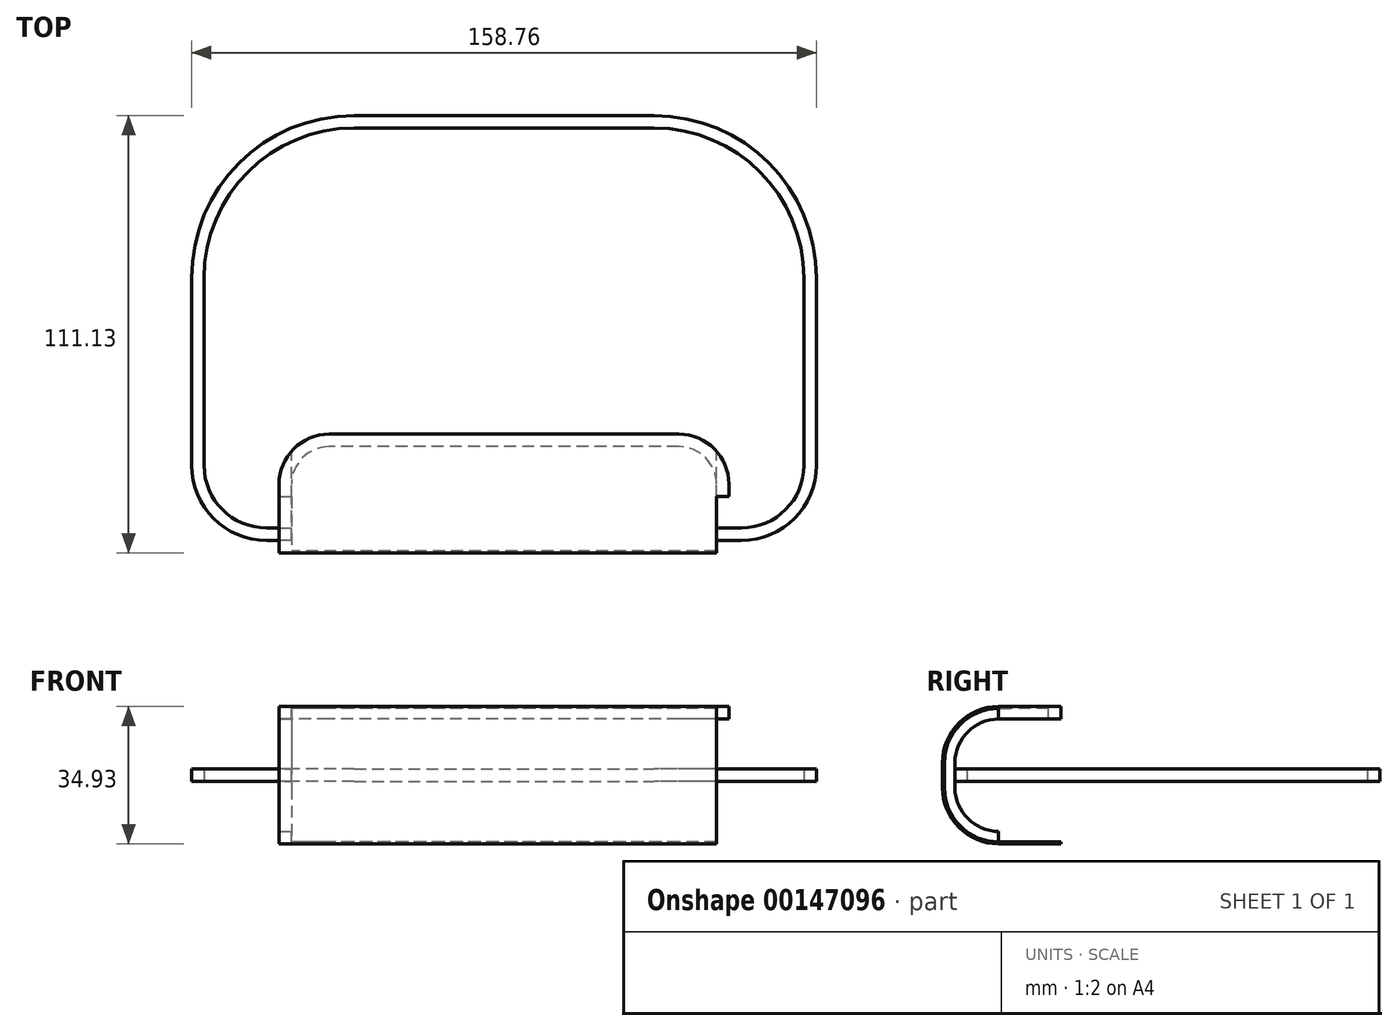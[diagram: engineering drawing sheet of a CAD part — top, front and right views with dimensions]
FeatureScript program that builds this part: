
annotation { "Feature Type Name" : "Feature", "Feature Type Description" : "" }
export const myFeature = defineFeature(function(context is Context, id is Id, definition is map)
    precondition{}
    {
        {
            var Q0;
            Q0=qCreatedBy(makeId("Top.planeOp"),FACE);
            var sketch = newSketch(context, id + "F0", { "sketchPlane" : qUnion([Q0])});
            skLineSegment(sketch, "E0.bottom", {"start": v(15.88, 0) * mm, "end": v(136.53, 0) * mm});
            skLineSegment(sketch, "E0.top", {"start": v(38.1, 101.6) * mm, "end": v(114.3, 101.6) * mm});
            skLineSegment(sketch, "E0.left", {"start": v(0, 15.87) * mm, "end": v(0, 63.5) * mm});
            skLineSegment(sketch, "E0.right", {"start": v(152.4, 15.88) * mm, "end": v(152.4, 63.5) * mm});
            skPoint(sketch, "E1.visualSharp", {"position": v(0, 101.6) * mm});
            skArc(sketch, "E1.filletArc", {"start": v(38.1, 101.6) * mm, "mid": v(11.16, 90.44) * mm, "end": v(0, 63.5) * mm});
            skPoint(sketch, "E2.visualSharp", {"position": v(152.4, 101.6) * mm});
            skArc(sketch, "E2.filletArc", {"start": v(152.4, 63.5) * mm, "mid": v(141.24, 90.44) * mm, "end": v(114.3, 101.6) * mm});
            skPoint(sketch, "E3.visualSharp", {"position": v(0, 0) * mm});
            skArc(sketch, "E3.filletArc", {"start": v(0, 15.87) * mm, "mid": v(4.65, 4.65) * mm, "end": v(15.87, 0) * mm});
            skPoint(sketch, "E4.visualSharp", {"position": v(152.4, 0) * mm});
            skArc(sketch, "E4.filletArc", {"start": v(136.53, 0) * mm, "mid": v(147.75, 4.65) * mm, "end": v(152.4, 15.88) * mm});
            skArc(sketch, "E5.0", {"start": v(38.1, 104.78) * mm, "mid": v(8.91, 92.69) * mm, "end": v(-3.18, 63.5) * mm});
            skArc(sketch, "E6.0", {"start": v(155.58, 63.5) * mm, "mid": v(143.49, 92.69) * mm, "end": v(114.3, 104.78) * mm});
            skArc(sketch, "E7.0", {"start": v(136.53, -3.18) * mm, "mid": v(150, 2.4) * mm, "end": v(155.58, 15.87) * mm});
            skArc(sketch, "E8.0", {"start": v(-3.18, 15.88) * mm, "mid": v(2.4, 2.4) * mm, "end": v(15.87, -3.18) * mm});
            skLineSegment(sketch, "E9", {"start": v(38.1, 104.78) * mm, "end": v(114.3, 104.78) * mm});
            skLineSegment(sketch, "E10", {"start": v(155.58, 63.5) * mm, "end": v(155.58, 15.87) * mm});
            skLineSegment(sketch, "E11", {"start": v(136.53, -3.18) * mm, "end": v(15.88, -3.18) * mm});
            skLineSegment(sketch, "E12", {"start": v(-3.18, 15.88) * mm, "end": v(-3.18, 63.5) * mm});
            skSolve(sketch);
        }
        {
            var Q0;
            Q0 = qSketchRegion(id + "F0", true);
            extrude(context, id + "F1", {"entities" : qUnion([Q0]), "depth" : 3.17 * mm});
        }
        {
            var Q0;
            Q0=makeQuery(id+"F1.opExtrude","CAP_FACE",FACE,{"disambiguationData":[OSD([sQuery(id+"F0.wireOp",EDGE,"E0.bottom"),sQuery(id+"F0.wireOp",EDGE,"E0.top"),sQuery(id+"F0.wireOp",EDGE,"E0.left"),sQuery(id+"F0.wireOp",EDGE,"E0.right"),sQuery(id+"F0.wireOp",EDGE,"E1.filletArc"),sQuery(id+"F0.wireOp",EDGE,"E2.filletArc"),sQuery(id+"F0.wireOp",EDGE,"E3.filletArc"),sQuery(id+"F0.wireOp",EDGE,"E4.filletArc"),sQuery(id+"F0.wireOp",EDGE,"E5.0"),sQuery(id+"F0.wireOp",EDGE,"E6.0"),sQuery(id+"F0.wireOp",EDGE,"E7.0"),sQuery(id+"F0.wireOp",EDGE,"E8.0"),sQuery(id+"F0.wireOp",EDGE,"E9"),sQuery(id+"F0.wireOp",EDGE,"E10"),sQuery(id+"F0.wireOp",EDGE,"E11"),sQuery(id+"F0.wireOp",EDGE,"E12")])],"isStart":false});
            var sketch = newSketch(context, id + "F2", { "sketchPlane" : qUnion([Q0])});
            skLineSegment(sketch, "E13.bottom", {"start": v(22.23, -3.18) * mm, "end": v(130.18, -3.18) * mm});
            skLineSegment(sketch, "E13.top", {"start": v(22.23, 0) * mm, "end": v(130.18, 0) * mm});
            skLineSegment(sketch, "E13.left", {"start": v(22.23, -3.18) * mm, "end": v(22.23, 0) * mm});
            skLineSegment(sketch, "E13.right", {"start": v(130.18, -3.18) * mm, "end": v(130.18, 0) * mm});
            skLineSegment(sketch, "E14", {"start": v(76.2, 101.6) * mm, "end": v(76.2, 0) * mm, "construction": true});
            skSolve(sketch);
        }
        {
            var Q0;
            Q0=makeQuery(id+"F2.imprint","IMPRINT",FACE,{"disambiguationData":[TD([[makeQuery(id+"F2.imprint","IMPRINT",EDGE,{"derivedFrom":sQuery(id+"F2.wireOp",EDGE,"E13.bottom")}),-1.0]])]});
            extrude(context, id + "F3", {"entities" : qUnion([Q0]), "operationType" : NewBodyOperationType.REMOVE, "endBound" : BoundingType.THROUGH_ALL, "oppositeDirection" : true, "depth" : 25.4 * mm});
        }
        {
            var Q0;
            Q0=makeQuery(id+"F3.boolean.opBoolean","COPY",FACE,{"derivedFrom":makeQuery(id+"F3.opExtrude","SWEPT_FACE",FACE,{"disambiguationData":[OSD([sQuery(id+"F2.wireOp",EDGE,"E13.left")])]})});
            var sketch = newSketch(context, id + "F4", { "sketchPlane" : qUnion([Q0])});
            skLineSegment(sketch, "E15", {"start": v(-3.18, 4.76) * mm, "end": v(-3.18, -1.59) * mm});
            skLineSegment(sketch, "E16", {"start": v(7.94, -12.7) * mm, "end": v(7.94, -12.7) * mm});
            skLineSegment(sketch, "E17", {"start": v(7.94, 15.88) * mm, "end": v(7.94, 15.88) * mm});
            skLineSegment(sketch, "E18", {"start": v(7.94, 15.88) * mm, "end": v(7.94, -12.7) * mm, "construction": true});
            skLineSegment(sketch, "E19", {"start": v(7.94, 15.88) * mm, "end": v(7.94, 19.05) * mm});
            skLineSegment(sketch, "E20", {"start": v(7.94, 19.05) * mm, "end": v(7.94, 19.05) * mm});
            skLineSegment(sketch, "E21", {"start": v(-6.35, 4.76) * mm, "end": v(-6.35, -1.59) * mm});
            skLineSegment(sketch, "E22", {"start": v(7.94, -15.88) * mm, "end": v(7.94, -15.88) * mm});
            skLineSegment(sketch, "E23", {"start": v(7.94, -15.88) * mm, "end": v(7.94, -12.7) * mm});
            skPoint(sketch, "E24.visualSharp", {"position": v(-3.18, 15.87) * mm});
            skArc(sketch, "E24.filletArc", {"start": v(7.94, 15.88) * mm, "mid": v(0.08, 12.62) * mm, "end": v(-3.18, 4.76) * mm});
            skPoint(sketch, "E25.visualSharp", {"position": v(-3.18, -12.7) * mm});
            skArc(sketch, "E25.filletArc", {"start": v(-3.18, -1.59) * mm, "mid": v(0.08, -9.45) * mm, "end": v(7.94, -12.7) * mm});
            skPoint(sketch, "E26.visualSharp", {"position": v(-6.35, 19.05) * mm});
            skArc(sketch, "E26.filletArc", {"start": v(7.94, 19.05) * mm, "mid": v(-2.17, 14.87) * mm, "end": v(-6.35, 4.76) * mm});
            skPoint(sketch, "E27.visualSharp", {"position": v(-6.35, -15.88) * mm});
            skArc(sketch, "E27.filletArc", {"start": v(-6.35, -1.59) * mm, "mid": v(-2.17, -11.7) * mm, "end": v(7.94, -15.87) * mm});
            skSolve(sketch);
        }
        {
            var Q0;
            Q0 = qSketchRegion(id + "F4", true);
            extrude(context, id + "F5", {"entities" : qUnion([Q0]), "operationType" : NewBodyOperationType.ADD, "oppositeDirection" : true, "depth" : 3.17 * mm});
        }
        {
            var Q0;
            Q0=makeQuery(id+"F1.opExtrude","CAP_FACE",FACE,{"disambiguationData":[OSD([sQuery(id+"F0.wireOp",EDGE,"E0.bottom"),sQuery(id+"F0.wireOp",EDGE,"E0.top"),sQuery(id+"F0.wireOp",EDGE,"E0.left"),sQuery(id+"F0.wireOp",EDGE,"E0.right"),sQuery(id+"F0.wireOp",EDGE,"E1.filletArc"),sQuery(id+"F0.wireOp",EDGE,"E2.filletArc"),sQuery(id+"F0.wireOp",EDGE,"E3.filletArc"),sQuery(id+"F0.wireOp",EDGE,"E4.filletArc"),sQuery(id+"F0.wireOp",EDGE,"E5.0"),sQuery(id+"F0.wireOp",EDGE,"E6.0"),sQuery(id+"F0.wireOp",EDGE,"E7.0"),sQuery(id+"F0.wireOp",EDGE,"E8.0"),sQuery(id+"F0.wireOp",EDGE,"E9"),sQuery(id+"F0.wireOp",EDGE,"E10"),sQuery(id+"F0.wireOp",EDGE,"E11"),sQuery(id+"F0.wireOp",EDGE,"E12")])],"isStart":false});
            var Q1;
            Q1=makeQuery(id+"F5.opExtrude","CAP_VERTEX",VERTEX,{"disambiguationData":[OSD([sQuery(id+"F4.wireOp",EDGE,"E19"),sQuery(id+"F4.wireOp",EDGE,"E26.filletArc")])],"isStart":true});
            cPlane(context, id + "F6", {"entities" : qUnion([Q0, Q1]), "cplaneType" : CPlaneType.PLANE_POINT, "offset" : 25.4 * mm, "width" : 152.4 * mm, "height" : 152.4 * mm});
        }
        {
            var Q0;
            Q0=makeQuery(id+"F5.boolean.opBoolean","MERGE",FACE,{"derivedFrom":[makeQuery(id+"F3.boolean.opBoolean","COPY",FACE,{"derivedFrom":makeQuery(id+"F3.opExtrude","SWEPT_FACE",FACE,{"disambiguationData":[OSD([sQuery(id+"F2.wireOp",EDGE,"E13.left")])]})}),makeQuery(id+"F5.opExtrude","CAP_FACE",FACE,{"disambiguationData":[OSD([sQuery(id+"F4.wireOp",EDGE,"E15"),sQuery(id+"F4.wireOp",EDGE,"E19"),sQuery(id+"F4.wireOp",EDGE,"E21"),sQuery(id+"F4.wireOp",EDGE,"E23"),sQuery(id+"F4.wireOp",EDGE,"E24.filletArc"),sQuery(id+"F4.wireOp",EDGE,"E25.filletArc"),sQuery(id+"F4.wireOp",EDGE,"E26.filletArc"),sQuery(id+"F4.wireOp",EDGE,"E27.filletArc")])],"isStart":true})]});
            var Q1;
            Q1=makeQuery(id+"F3.boolean.opBoolean","COPY",FACE,{"derivedFrom":makeQuery(id+"F3.opExtrude","SWEPT_FACE",FACE,{"disambiguationData":[OSD([sQuery(id+"F2.wireOp",EDGE,"E13.right")])]})});
            cPlane(context, id + "F7", {"entities" : qUnion([Q0, Q1]), "cplaneType" : CPlaneType.MID_PLANE, "offset" : 25.4 * mm, "width" : 152.4 * mm, "height" : 152.4 * mm});
        }
        {
            var Q0;
            Q0=qCreatedBy(id+"F6.planeOp",FACE);
            var sketch = newSketch(context, id + "F8", { "sketchPlane" : qUnion([Q0])});
            skArc(sketch, "E28", {"start": v(31.75, 20.64) * mm, "mid": v(25.01, 17.85) * mm, "end": v(22.23, 11.11) * mm});
            skArc(sketch, "E29", {"start": v(130.18, 11.11) * mm, "mid": v(127.39, 17.85) * mm, "end": v(120.65, 20.64) * mm});
            skArc(sketch, "E30", {"start": v(31.75, 23.81) * mm, "mid": v(22.77, 20.1) * mm, "end": v(19.05, 11.11) * mm});
            skArc(sketch, "E31", {"start": v(133.35, 11.11) * mm, "mid": v(129.63, 20.1) * mm, "end": v(120.65, 23.81) * mm});
            skLineSegment(sketch, "E32", {"start": v(31.75, 20.64) * mm, "end": v(120.65, 20.64) * mm});
            skLineSegment(sketch, "E33", {"start": v(120.65, 23.81) * mm, "end": v(31.75, 23.81) * mm});
            skLineSegment(sketch, "E34", {"start": v(19.05, 7.94) * mm, "end": v(22.23, 7.94) * mm});
            skLineSegment(sketch, "E35", {"start": v(22.23, 7.94) * mm, "end": v(22.23, 11.11) * mm});
            skLineSegment(sketch, "E36", {"start": v(19.05, 7.94) * mm, "end": v(19.05, 11.11) * mm});
            skLineSegment(sketch, "E37", {"start": v(130.18, 7.94) * mm, "end": v(133.35, 7.94) * mm});
            skLineSegment(sketch, "E38", {"start": v(133.35, 7.94) * mm, "end": v(133.35, 11.11) * mm});
            skLineSegment(sketch, "E39", {"start": v(130.18, 7.94) * mm, "end": v(130.18, 11.11) * mm});
            skSolve(sketch);
        }
        {
            var Q0;
            Q0=makeQuery(id+"F8.imprint","IMPRINT",FACE,{"disambiguationData":[TD([[makeQuery(id+"F8.imprint","IMPRINT",EDGE,{"derivedFrom":sQuery(id+"F8.wireOp",EDGE,"E28")}),-1.0]])]});
            extrude(context, id + "F9", {"entities" : qUnion([Q0]), "operationType" : NewBodyOperationType.ADD, "oppositeDirection" : true, "depth" : 3.17 * mm});
        }
        {
            var Q0;
            Q0=makeQuery(id+"F1.opExtrude","CAP_FACE",FACE,{"disambiguationData":[OSD([sQuery(id+"F0.wireOp",EDGE,"E0.bottom"),sQuery(id+"F0.wireOp",EDGE,"E0.top"),sQuery(id+"F0.wireOp",EDGE,"E0.left"),sQuery(id+"F0.wireOp",EDGE,"E0.right"),sQuery(id+"F0.wireOp",EDGE,"E1.filletArc"),sQuery(id+"F0.wireOp",EDGE,"E2.filletArc"),sQuery(id+"F0.wireOp",EDGE,"E3.filletArc"),sQuery(id+"F0.wireOp",EDGE,"E4.filletArc"),sQuery(id+"F0.wireOp",EDGE,"E5.0"),sQuery(id+"F0.wireOp",EDGE,"E6.0"),sQuery(id+"F0.wireOp",EDGE,"E7.0"),sQuery(id+"F0.wireOp",EDGE,"E8.0"),sQuery(id+"F0.wireOp",EDGE,"E9"),sQuery(id+"F0.wireOp",EDGE,"E10"),sQuery(id+"F0.wireOp",EDGE,"E11"),sQuery(id+"F0.wireOp",EDGE,"E12")])],"isStart":false});
            var Q1;
            Q1=makeQuery(id+"F1.opExtrude","CAP_FACE",FACE,{"disambiguationData":[OSD([sQuery(id+"F0.wireOp",EDGE,"E0.bottom"),sQuery(id+"F0.wireOp",EDGE,"E0.top"),sQuery(id+"F0.wireOp",EDGE,"E0.left"),sQuery(id+"F0.wireOp",EDGE,"E0.right"),sQuery(id+"F0.wireOp",EDGE,"E1.filletArc"),sQuery(id+"F0.wireOp",EDGE,"E2.filletArc"),sQuery(id+"F0.wireOp",EDGE,"E3.filletArc"),sQuery(id+"F0.wireOp",EDGE,"E4.filletArc"),sQuery(id+"F0.wireOp",EDGE,"E5.0"),sQuery(id+"F0.wireOp",EDGE,"E6.0"),sQuery(id+"F0.wireOp",EDGE,"E7.0"),sQuery(id+"F0.wireOp",EDGE,"E8.0"),sQuery(id+"F0.wireOp",EDGE,"E9"),sQuery(id+"F0.wireOp",EDGE,"E10"),sQuery(id+"F0.wireOp",EDGE,"E11"),sQuery(id+"F0.wireOp",EDGE,"E12")])],"isStart":true});
            cPlane(context, id + "F10", {"entities" : qUnion([Q0, Q1]), "cplaneType" : CPlaneType.MID_PLANE, "offset" : 25.4 * mm, "width" : 152.4 * mm, "height" : 152.4 * mm});
        }
        {
            var Q0;
            Q0=makeQuery(id+"F5.boolean.opBoolean","MERGE",FACE,{"derivedFrom":[makeQuery(id+"F3.boolean.opBoolean","COPY",FACE,{"derivedFrom":makeQuery(id+"F3.opExtrude","SWEPT_FACE",FACE,{"disambiguationData":[OSD([sQuery(id+"F2.wireOp",EDGE,"E13.left")])]})}),makeQuery(id+"F5.opExtrude","CAP_FACE",FACE,{"disambiguationData":[OSD([sQuery(id+"F4.wireOp",EDGE,"E15"),sQuery(id+"F4.wireOp",EDGE,"E19"),sQuery(id+"F4.wireOp",EDGE,"E21"),sQuery(id+"F4.wireOp",EDGE,"E23"),sQuery(id+"F4.wireOp",EDGE,"E24.filletArc"),sQuery(id+"F4.wireOp",EDGE,"E25.filletArc"),sQuery(id+"F4.wireOp",EDGE,"E26.filletArc"),sQuery(id+"F4.wireOp",EDGE,"E27.filletArc")])],"isStart":true})]});
            var sketch = newSketch(context, id + "F11", { "sketchPlane" : qUnion([Q0])});
            skArc(sketch, "E40", {"start": v(7.94, 19.05) * mm, "mid": v(-2.17, 14.87) * mm, "end": v(-6.35, 4.76) * mm});
            skArc(sketch, "E41", {"start": v(-5.84, -1.59) * mm, "mid": v(-1.8, -11.33) * mm, "end": v(7.94, -15.37) * mm});
            skArc(sketch, "E42", {"start": v(-6.35, -1.59) * mm, "mid": v(-2.17, -11.7) * mm, "end": v(7.94, -15.87) * mm});
            skLineSegment(sketch, "E43", {"start": v(-6.35, 4.76) * mm, "end": v(-6.35, -1.59) * mm});
            skLineSegment(sketch, "E44", {"start": v(7.94, -15.87) * mm, "end": v(23.81, -15.87) * mm});
            skLineSegment(sketch, "E45", {"start": v(7.94, 19.05) * mm, "end": v(23.81, 19.05) * mm});
            skLineSegment(sketch, "E46.0", {"start": v(7.94, 18.54) * mm, "end": v(23.81, 18.54) * mm});
            skLineSegment(sketch, "E47.0", {"start": v(7.94, -15.37) * mm, "end": v(23.81, -15.37) * mm});
            skLineSegment(sketch, "E48", {"start": v(23.81, 19.05) * mm, "end": v(23.81, 18.54) * mm});
            skLineSegment(sketch, "E49", {"start": v(23.81, 18.54) * mm, "end": v(23.81, -15.37) * mm, "construction": true});
            skLineSegment(sketch, "E50", {"start": v(23.81, -15.37) * mm, "end": v(23.81, -15.87) * mm});
            skLineSegment(sketch, "E51.0", {"start": v(-5.84, 4.76) * mm, "end": v(-5.84, -1.59) * mm});
            skArc(sketch, "E52.trimOffspring", {"start": v(7.94, 18.54) * mm, "mid": v(-1.8, 14.5) * mm, "end": v(-5.84, 4.76) * mm});
            skSolve(sketch);
        }
        {
            var Q0;
            Q0 = qSketchRegion(id + "F11", true);
            var Q1;
            Q1=makeQuery(id+"FOcBKYxvywjC2zy_1.1.F5.boolean.opBoolean","MERGE",FACE,{"derivedFrom":[makeQuery(id+"F3.boolean.opBoolean","COPY",FACE,{"derivedFrom":makeQuery(id+"F3.opExtrude","SWEPT_FACE",FACE,{"disambiguationData":[OSD([sQuery(id+"F2.wireOp",EDGE,"E13.right")])]})}),makeQuery(id+"FOcBKYxvywjC2zy_1.1.F5.opExtrude","CAP_FACE",FACE,{"disambiguationData":[OSD([sQuery(id+"F4.wireOp",EDGE,"E15"),sQuery(id+"F4.wireOp",EDGE,"E19"),sQuery(id+"F4.wireOp",EDGE,"E21"),sQuery(id+"F4.wireOp",EDGE,"E23"),sQuery(id+"F4.wireOp",EDGE,"E24.filletArc"),sQuery(id+"F4.wireOp",EDGE,"E25.filletArc"),sQuery(id+"F4.wireOp",EDGE,"E26.filletArc"),sQuery(id+"F4.wireOp",EDGE,"E27.filletArc")])],"isStart":true})]});
            extrude(context, id + "F12", {"entities" : qUnion([Q0]), "operationType" : NewBodyOperationType.ADD, "endBound" : BoundingType.UP_TO_SURFACE, "endBoundEntityFace" : qUnion([Q1]), "depth" : 25.4 * mm});
        }
        {
            var Q0;
            Q0=makeQuery(id+"F12.boolean.opBoolean","MERGE",FACE,{"derivedFrom":[makeQuery(id+"F9.opExtrude","CAP_FACE",FACE,{"disambiguationData":[OSD([sQuery(id+"F8.wireOp",EDGE,"E28"),sQuery(id+"F8.wireOp",EDGE,"E29"),sQuery(id+"F8.wireOp",EDGE,"E30"),sQuery(id+"F8.wireOp",EDGE,"E31"),sQuery(id+"F8.wireOp",EDGE,"RZO0rK6G-VcWh-IXgy-n1za-RGXm0N0zLf3t"),sQuery(id+"F8.wireOp",EDGE,"5kI8PMHy-GDlY-gytp-9yt7-23ZE9qi01Bs5"),sQuery(id+"F8.wireOp",EDGE,"E32"),sQuery(id+"F8.wireOp",EDGE,"E33")])],"isStart":true}),makeQuery(id+"F12.opExtrude","SWEPT_FACE",FACE,{"disambiguationData":[OSD([sQuery(id+"F11.wireOp",EDGE,"E45")])]})]});
            var sketch = newSketch(context, id + "F13", { "sketchPlane" : qUnion([Q0])});
            skArc(sketch, "E53", {"start": v(31.75, 23.81) * mm, "mid": v(26.52, 22.69) * mm, "end": v(22.23, 19.51) * mm});
            skArc(sketch, "E54", {"start": v(130.17, 19.51) * mm, "mid": v(125.88, 22.69) * mm, "end": v(120.65, 23.81) * mm});
            skLineSegment(sketch, "E55", {"start": v(22.23, 23.81) * mm, "end": v(22.23, 19.51) * mm});
            skLineSegment(sketch, "E56", {"start": v(22.23, 23.81) * mm, "end": v(31.75, 23.81) * mm});
            skLineSegment(sketch, "E57", {"start": v(130.18, 23.81) * mm, "end": v(120.65, 23.81) * mm});
            skLineSegment(sketch, "E58", {"start": v(130.18, 23.81) * mm, "end": v(130.18, 19.51) * mm});
            skSolve(sketch);
        }
        {
            var Q0;
            Q0 = qSketchRegion(id + "F13", true);
            extrude(context, id + "F14", {"entities" : qUnion([Q0]), "operationType" : NewBodyOperationType.REMOVE, "endBound" : BoundingType.THROUGH_ALL, "oppositeDirection" : true, "depth" : 25.4 * mm});
        }
    });
